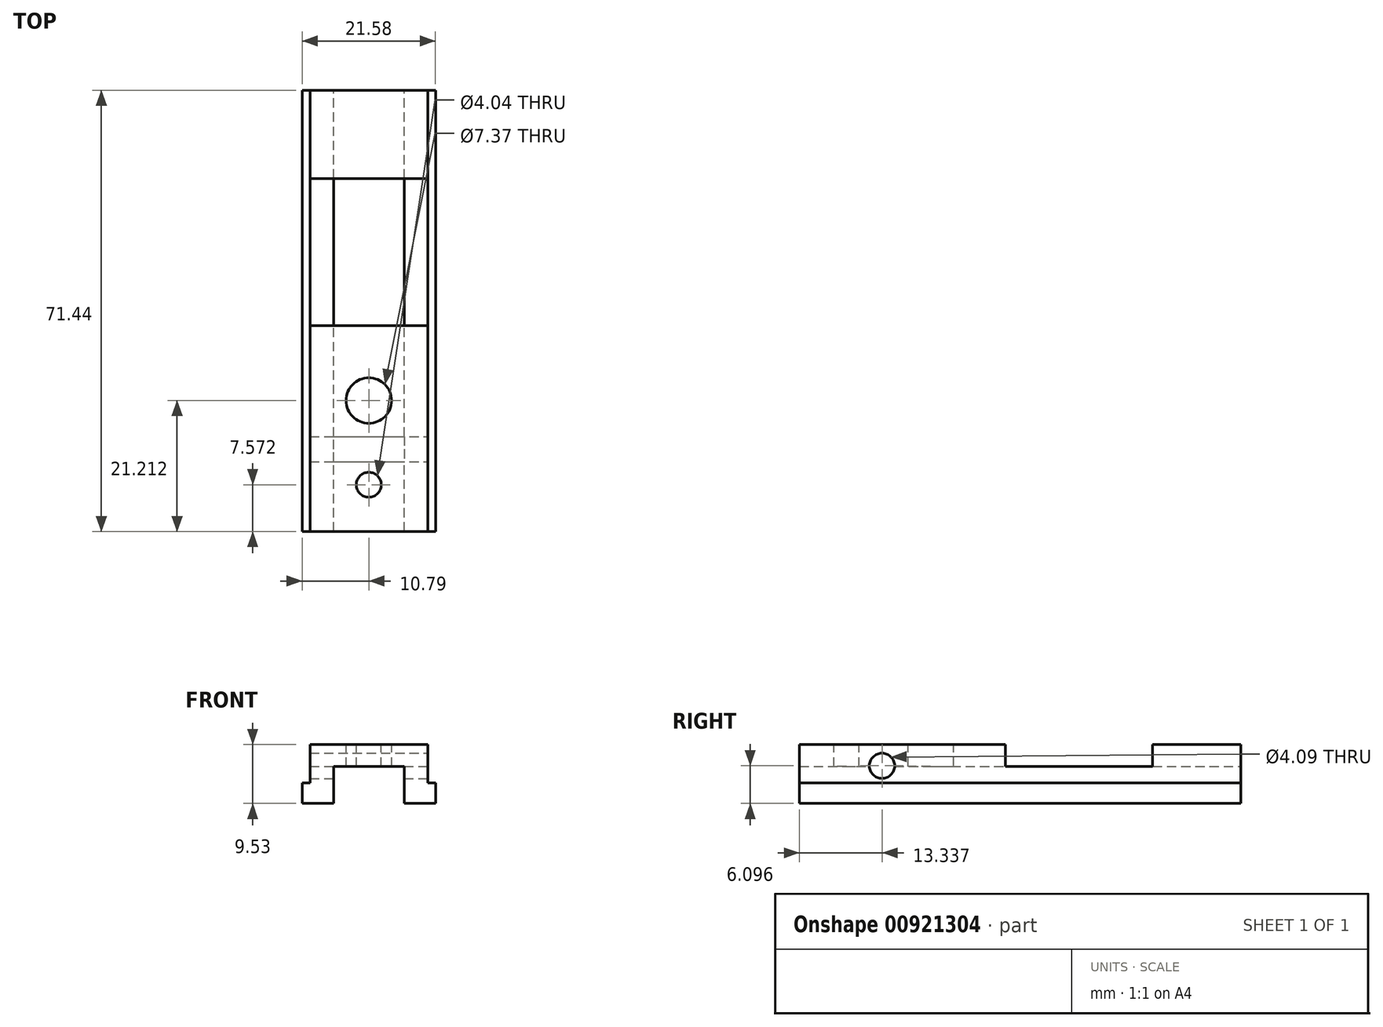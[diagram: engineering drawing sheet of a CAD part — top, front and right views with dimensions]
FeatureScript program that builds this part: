
annotation { "Feature Type Name" : "Feature", "Feature Type Description" : "" }
export const myFeature = defineFeature(function(context is Context, id is Id, definition is map)
    precondition{}
    {
        {
            var Q0;
            Q0=qCreatedBy(makeId("Front.planeOp"),FACE);
            var sketch = newSketch(context, id + "F0", { "sketchPlane" : qUnion([Q0])});
            skLineSegment(sketch, "E0", {"start": v(-9.53, 9.52) * mm, "end": v(9.52, 9.52) * mm});
            skLineSegment(sketch, "E1", {"start": v(9.52, 9.52) * mm, "end": v(9.52, 3.3) * mm});
            skLineSegment(sketch, "E2", {"start": v(9.53, 3.3) * mm, "end": v(10.8, 3.3) * mm});
            skLineSegment(sketch, "E3", {"start": v(10.8, 3.3) * mm, "end": v(10.8, 0) * mm});
            skLineSegment(sketch, "E4", {"start": v(10.8, 0) * mm, "end": v(5.71, 0) * mm});
            skLineSegment(sketch, "E5", {"start": v(5.71, 0) * mm, "end": v(5.71, 5.97) * mm});
            skLineSegment(sketch, "E6", {"start": v(5.72, 5.97) * mm, "end": v(-5.72, 5.97) * mm});
            skLineSegment(sketch, "E7", {"start": v(-5.72, 5.97) * mm, "end": v(-5.72, 0) * mm});
            skLineSegment(sketch, "E8", {"start": v(-5.72, 0) * mm, "end": v(-10.8, 0) * mm});
            skLineSegment(sketch, "E9", {"start": v(-10.8, 0) * mm, "end": v(-10.8, 3.3) * mm});
            skLineSegment(sketch, "E10", {"start": v(-10.8, 3.3) * mm, "end": v(-9.53, 3.3) * mm});
            skLineSegment(sketch, "E11", {"start": v(-9.53, 3.3) * mm, "end": v(-9.53, 9.52) * mm});
            skSolve(sketch);
        }
        {
            var Q0;
            Q0 = qSketchRegion(id + "F0", true);
            extrude(context, id + "F1", {"entities" : qUnion([Q0]), "depth" : 71.44 * mm, "offsetDistance" : 25.4 * mm});
        }
        {
            var Q0;
            Q0=makeQuery(id+"F1.opExtrude","SWEPT_FACE",FACE,{"disambiguationData":[OSD([sQuery(id+"F0.wireOp",EDGE,"E0")])]});
            var sketch = newSketch(context, id + "F2", { "sketchPlane" : qUnion([Q0])});
            skCircle(sketch, "E12", {"center": v(0, -50.23) * mm, "radius": 3.68 * mm});
            skCircle(sketch, "E13", {"center": v(0, -63.87) * mm, "radius": 2.02 * mm});
            skSolve(sketch);
        }
        {
            var Q0;
            Q0 = qSketchRegion(id + "F2", true);
            extrude(context, id + "F3", {"entities" : qUnion([Q0]), "operationType" : NewBodyOperationType.REMOVE, "endBound" : BoundingType.THROUGH_ALL, "oppositeDirection" : true, "depth" : 25.4 * mm, "offsetDistance" : 25.4 * mm});
        }
        {
            var Q0;
            Q0=makeQuery(id+"F1.opExtrude","SWEPT_FACE",FACE,{"disambiguationData":[OSD([sQuery(id+"F0.wireOp",EDGE,"E1")])]});
            var sketch = newSketch(context, id + "F4", { "sketchPlane" : qUnion([Q0])});
            skCircle(sketch, "E14", {"center": v(-58.1, 6.1) * mm, "radius": 2.04 * mm});
            skSolve(sketch);
        }
        {
            var Q0;
            Q0=makeQuery(id+"F4.imprint","IMPRINT",FACE,{"disambiguationData":[TD([[makeQuery(id+"F4.imprint","IMPRINT",EDGE,{"derivedFrom":sQuery(id+"F4.wireOp",EDGE,"E14")}),1.0]])]});
            extrude(context, id + "F5", {"entities" : qUnion([Q0]), "operationType" : NewBodyOperationType.REMOVE, "endBound" : BoundingType.THROUGH_ALL, "oppositeDirection" : true, "depth" : 4.44 * mm, "offsetDistance" : 25.4 * mm});
        }
        {
            var Q0;
            Q0=makeQuery(id+"F1.opExtrude","SWEPT_FACE",FACE,{"disambiguationData":[OSD([sQuery(id+"F0.wireOp",EDGE,"E0")])]});
            var sketch = newSketch(context, id + "F6", { "sketchPlane" : qUnion([Q0])});
            skLineSegment(sketch, "E15.bottom", {"start": v(-9.53, -14.29) * mm, "end": v(9.52, -14.29) * mm});
            skLineSegment(sketch, "E15.top", {"start": v(-9.53, -38.1) * mm, "end": v(9.52, -38.1) * mm});
            skLineSegment(sketch, "E15.left", {"start": v(-9.53, -14.29) * mm, "end": v(-9.53, -38.1) * mm});
            skLineSegment(sketch, "E15.right", {"start": v(9.52, -14.29) * mm, "end": v(9.52, -38.1) * mm});
            skSolve(sketch);
        }
        {
            var Q0;
            Q0=makeQuery(id+"F6.imprint","IMPRINT",FACE,{"disambiguationData":[TD([[makeQuery(id+"F6.imprint","IMPRINT",EDGE,{"derivedFrom":sQuery(id+"F6.wireOp",EDGE,"E15.bottom")}),-1.0]])]});
            extrude(context, id + "F7", {"entities" : qUnion([Q0]), "operationType" : NewBodyOperationType.REMOVE, "oppositeDirection" : true, "depth" : 3.56 * mm, "offsetDistance" : 25.4 * mm});
        }
    });
